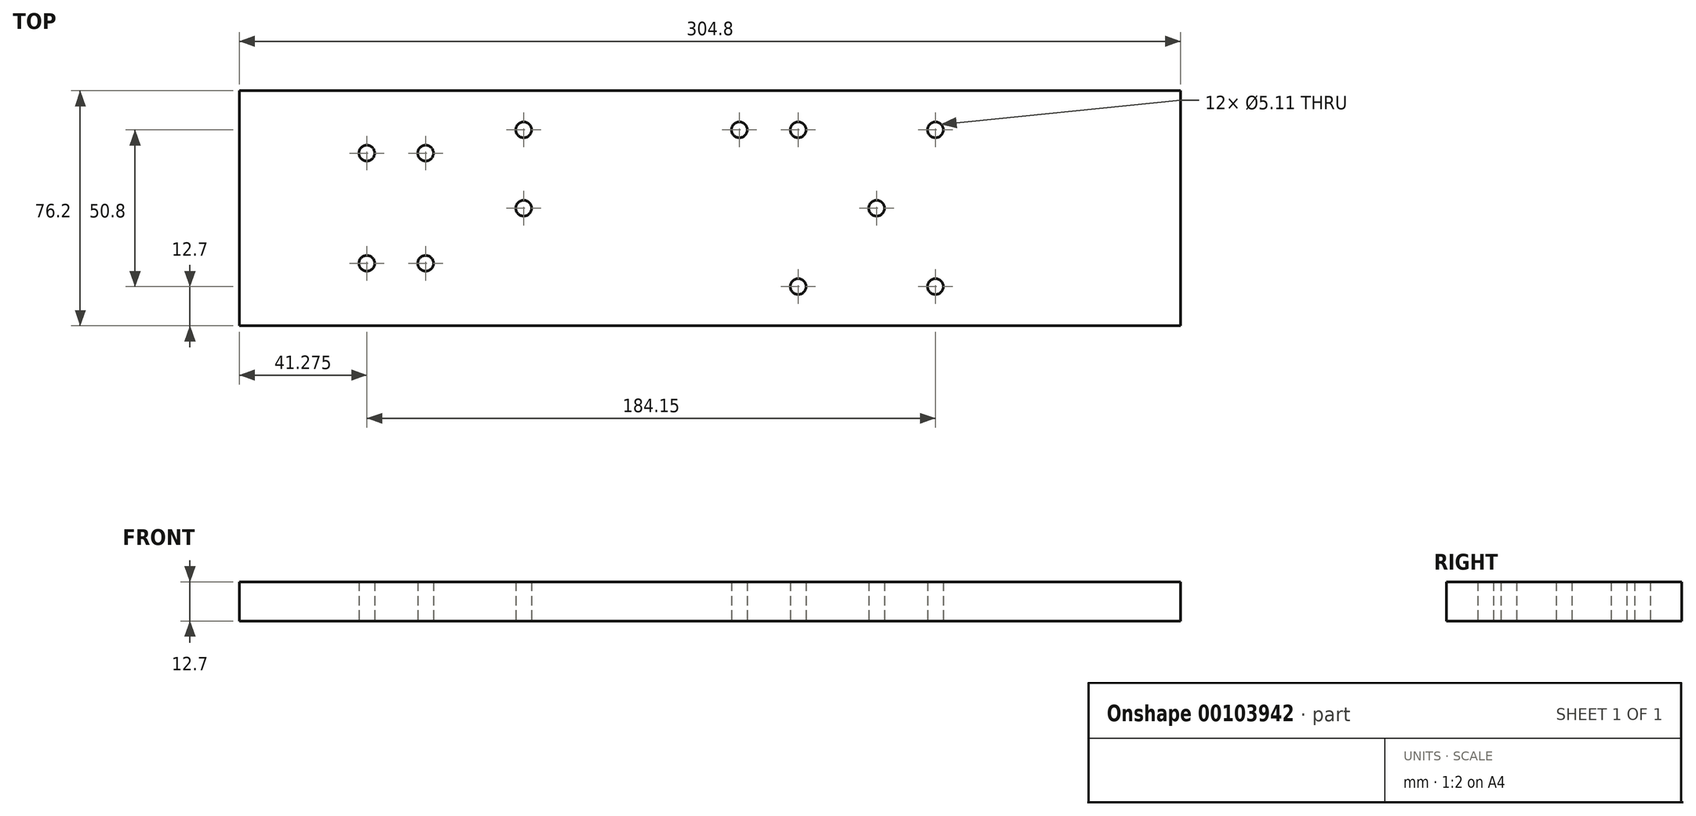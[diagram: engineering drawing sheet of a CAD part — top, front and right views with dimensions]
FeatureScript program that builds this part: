
annotation { "Feature Type Name" : "Feature", "Feature Type Description" : "" }
export const myFeature = defineFeature(function(context is Context, id is Id, definition is map)
    precondition{}
    {
        {
            var Q0;
            Q0=qCreatedBy(makeId("Top.planeOp"),FACE);
            var sketch = newSketch(context, id + "F0", { "sketchPlane" : qUnion([Q0])});
            skLineSegment(sketch, "E0.bottom", {"start": v(0, 0) * mm, "end": v(285.75, 0) * mm});
            skLineSegment(sketch, "E0.top", {"start": v(44.45, -76.2) * mm, "end": v(285.75, -76.2) * mm});
            skLineSegment(sketch, "E0.right", {"start": v(285.75, 0) * mm, "end": v(285.75, -76.2) * mm});
            skCircle(sketch, "E1", {"center": v(73.03, -12.7) * mm, "radius": 4.76 * mm, "construction": true});
            skCircle(sketch, "E2", {"center": v(142.88, -12.7) * mm, "radius": 4.76 * mm, "construction": true});
            skLineSegment(sketch, "E3.bottom", {"start": v(53.98, -19.05) * mm, "end": v(180.98, -19.05) * mm, "construction": true});
            skLineSegment(sketch, "E3.top", {"start": v(53.98, -57.15) * mm, "end": v(180.98, -57.15) * mm, "construction": true});
            skLineSegment(sketch, "E3.left", {"start": v(53.98, -19.05) * mm, "end": v(53.98, -57.15) * mm, "construction": true});
            skLineSegment(sketch, "E3.right", {"start": v(180.98, -19.05) * mm, "end": v(180.98, -57.15) * mm, "construction": true});
            skLineSegment(sketch, "E4", {"start": v(-19.05, -38.1) * mm, "end": v(285.75, -38.1) * mm, "construction": true});
            skPoint(sketch, "E5", {"position": v(53.98, -38.1) * mm});
            skCircle(sketch, "E6", {"center": v(73.03, -38.1) * mm, "radius": 4.17 * mm, "construction": true});
            skCircle(sketch, "E7", {"center": v(161.93, -38.1) * mm, "radius": 4.17 * mm, "construction": true});
            skCircle(sketch, "E8", {"center": v(73.03, -12.7) * mm, "radius": 2.55 * mm});
            skCircle(sketch, "E9", {"center": v(142.88, -12.7) * mm, "radius": 2.55 * mm});
            skCircle(sketch, "E10", {"center": v(22.23, -20.24) * mm, "radius": 2.55 * mm});
            skCircle(sketch, "E11", {"center": v(41.28, -20.24) * mm, "radius": 2.55 * mm});
            skCircle(sketch, "E12.MirrorC", {"center": v(22.23, -55.96) * mm, "radius": 2.55 * mm});
            skCircle(sketch, "E13.MirrorC", {"center": v(41.28, -55.96) * mm, "radius": 2.55 * mm});
            skCircle(sketch, "E14", {"center": v(187.33, -38.1) * mm, "radius": 4.76 * mm, "construction": true});
            skCircle(sketch, "E15", {"center": v(187.33, -38.1) * mm, "radius": 2.55 * mm});
            skCircle(sketch, "E16", {"center": v(206.38, -12.7) * mm, "radius": 2.55 * mm});
            skLineSegment(sketch, "E17", {"start": v(206.38, -12.7) * mm, "end": v(206.38, -66.68) * mm, "construction": true});
            skLineSegment(sketch, "E18.0", {"start": v(198.44, -9.52) * mm, "end": v(198.44, -66.67) * mm, "construction": true});
            skLineSegment(sketch, "E19.0", {"start": v(214.31, -9.52) * mm, "end": v(214.31, -66.67) * mm, "construction": true});
            skCircle(sketch, "E20", {"center": v(73.03, -12.7) * mm, "radius": 6.35 * mm, "construction": true});
            skCircle(sketch, "E21", {"center": v(142.88, -12.7) * mm, "radius": 6.35 * mm, "construction": true});
            skCircle(sketch, "E22", {"center": v(187.33, -38.1) * mm, "radius": 6.35 * mm, "construction": true});
            skCircle(sketch, "E23.MirrorC", {"center": v(206.38, -63.5) * mm, "radius": 2.55 * mm});
            skCircle(sketch, "E24", {"center": v(161.93, -12.7) * mm, "radius": 2.55 * mm});
            skCircle(sketch, "E25.MirrorC", {"center": v(161.93, -63.5) * mm, "radius": 2.55 * mm});
            skCircle(sketch, "E26", {"center": v(73.03, -38.1) * mm, "radius": 2.55 * mm});
            skLineSegment(sketch, "E27", {"start": v(0, 0) * mm, "end": v(-19.05, 0) * mm});
            skLineSegment(sketch, "E28", {"start": v(-19.05, 0) * mm, "end": v(-19.05, -76.2) * mm});
            skLineSegment(sketch, "E29", {"start": v(44.45, -76.2) * mm, "end": v(-19.05, -76.2) * mm});
            skPoint(sketch, "E30.orphan", {"position": v(22.22, -38.1) * mm});
            skSolve(sketch);
        }
        {
            var Q0;
            Q0=qSketchRegion(id+"F0",true);
            extrude(context, id + "F1", {"entities" : qUnion([Q0]), "depth" : 12.7 * mm});
        }
    });
